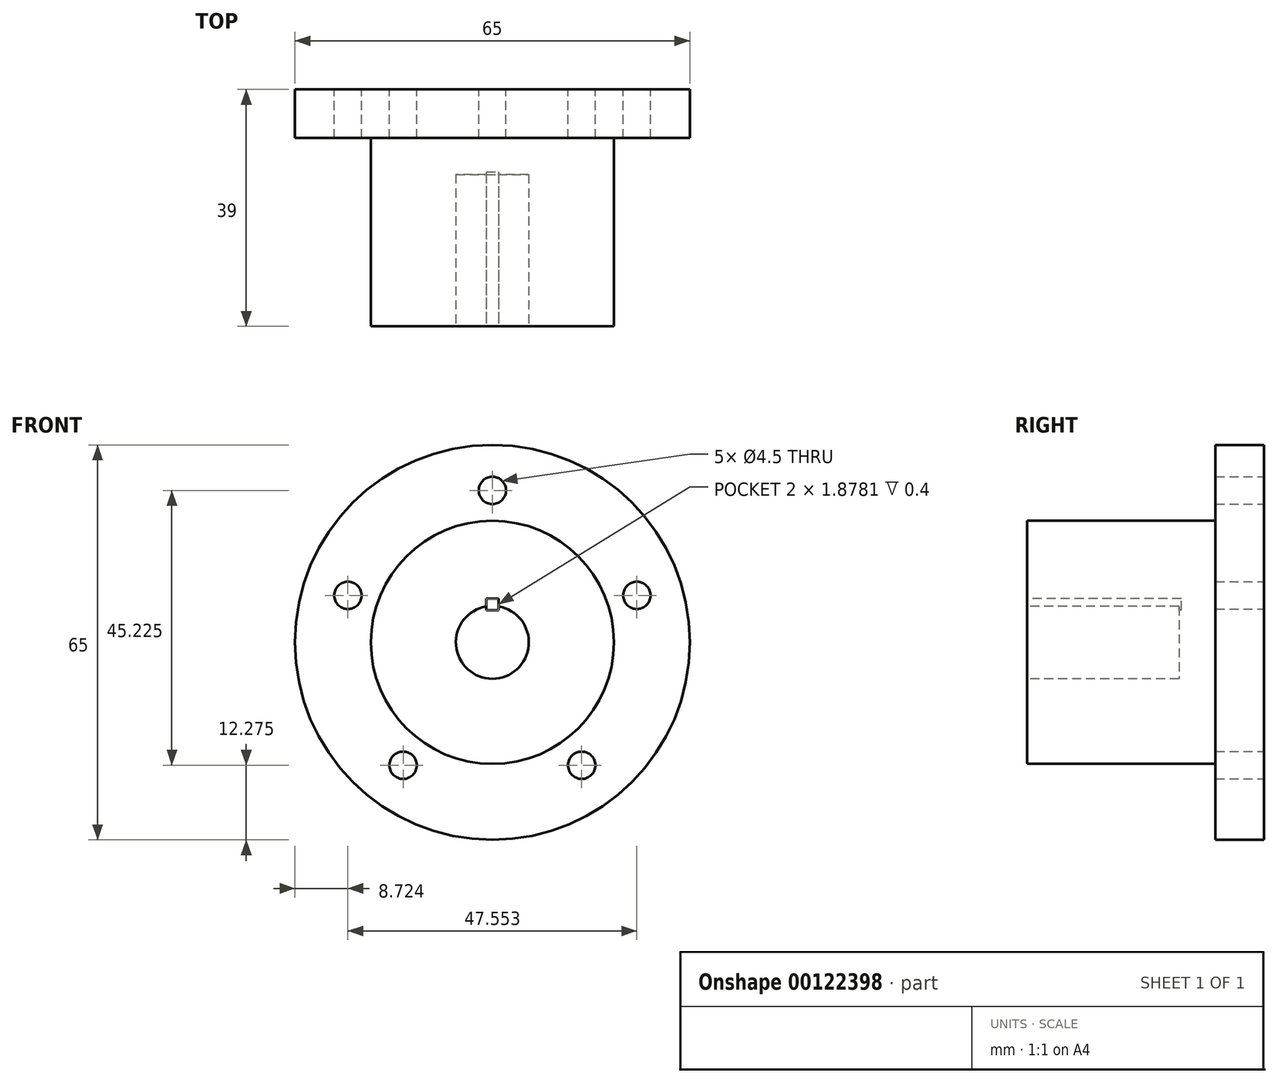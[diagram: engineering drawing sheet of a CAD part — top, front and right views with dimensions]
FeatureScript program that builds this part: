
annotation { "Feature Type Name" : "Feature", "Feature Type Description" : "" }
export const myFeature = defineFeature(function(context is Context, id is Id, definition is map)
    precondition{}
    {
        {
            var Q0;
            Q0=qCreatedBy(makeId("Front.planeOp"),FACE);
            var sketch = newSketch(context, id + "F0", { "sketchPlane" : qUnion([Q0])});
            skCircle(sketch, "E0", {"center": v(0, 0) * mm, "radius": 32.5 * mm});
            skSolve(sketch);
        }
        {
            var Q0;
            Q0=makeQuery(id+"F0.imprint","IMPRINT",FACE,{"disambiguationData":[TD([[makeQuery(id+"F0.imprint","IMPRINT",EDGE,{"derivedFrom":sQuery(id+"F0.wireOp",EDGE,"E0")}),1.0]])]});
            extrude(context, id + "F1", {"entities" : qUnion([Q0]), "depth" : 8 * mm});
        }
        {
            var Q0;
            Q0=makeQuery(id+"F1.opExtrude","CAP_FACE",FACE,{"disambiguationData":[OSD([sQuery(id+"F0.wireOp",EDGE,"E0")])],"isStart":false});
            var sketch = newSketch(context, id + "F2", { "sketchPlane" : qUnion([Q0])});
            skCircle(sketch, "E1", {"center": v(0, 0) * mm, "radius": 20 * mm});
            skSolve(sketch);
        }
        {
            var Q0;
            Q0=makeQuery(id+"F2.imprint","IMPRINT",FACE,{"disambiguationData":[TD([[makeQuery(id+"F2.imprint","IMPRINT",EDGE,{"derivedFrom":sQuery(id+"F2.wireOp",EDGE,"E1")}),1.0]])]});
            extrude(context, id + "F3", {"entities" : qUnion([Q0]), "operationType" : NewBodyOperationType.ADD, "depth" : 31 * mm});
        }
        {
            var Q0;
            Q0=makeQuery(id+"F3.opExtrude","CAP_FACE",FACE,{"disambiguationData":[OSD([sQuery(id+"F2.wireOp",EDGE,"E1")])],"isStart":false});
            var sketch = newSketch(context, id + "F4", { "sketchPlane" : qUnion([Q0])});
            skCircle(sketch, "E2", {"center": v(0, 0) * mm, "radius": 6 * mm});
            skSolve(sketch);
        }
        {
            var Q0;
            Q0=makeQuery(id+"F4.imprint","IMPRINT",FACE,{"disambiguationData":[TD([[makeQuery(id+"F4.imprint","IMPRINT",EDGE,{"derivedFrom":sQuery(id+"F4.wireOp",EDGE,"E2")}),1.0]])]});
            extrude(context, id + "F5", {"entities" : qUnion([Q0]), "operationType" : NewBodyOperationType.REMOVE, "oppositeDirection" : true, "depth" : 25 * mm});
        }
        {
            var Q0;
            Q0=makeQuery(id+"F3.opExtrude","CAP_FACE",FACE,{"disambiguationData":[OSD([sQuery(id+"F2.wireOp",EDGE,"E1")])],"isStart":false});
            var sketch = newSketch(context, id + "F6", { "sketchPlane" : qUnion([Q0])});
            skCircle(sketch, "E3.0", {"center": v(0, 0) * mm, "radius": 6 * mm, "construction": true});
            skLineSegment(sketch, "E4", {"start": v(0, 0) * mm, "end": v(0, 6) * mm, "construction": true});
            skLineSegment(sketch, "E5", {"start": v(0, 5.29) * mm, "end": v(1, 5.29) * mm});
            skLineSegment(sketch, "E6", {"start": v(1, 5.29) * mm, "end": v(1, 7.17) * mm});
            skLineSegment(sketch, "E7", {"start": v(0, 5.29) * mm, "end": v(-1, 5.29) * mm});
            skLineSegment(sketch, "E8", {"start": v(-1, 5.29) * mm, "end": v(-1, 7.17) * mm});
            skLineSegment(sketch, "E9", {"start": v(-1, 7.17) * mm, "end": v(1, 7.17) * mm});
            skSolve(sketch);
        }
        {
            var Q0;
            Q0 = qSketchRegion(id + "F6", true);
            extrude(context, id + "F7", {"entities" : qUnion([Q0]), "operationType" : NewBodyOperationType.REMOVE, "oppositeDirection" : true, "depth" : 25.4 * mm});
        }
        {
            var Q0;
            Q0=makeQuery(id+"F1.opExtrude","CAP_FACE",FACE,{"disambiguationData":[OSD([sQuery(id+"F0.wireOp",EDGE,"E0")])],"isStart":true});
            var sketch = newSketch(context, id + "F8", { "sketchPlane" : qUnion([Q0])});
            skLineSegment(sketch, "E10", {"start": v(0, 0) * mm, "end": v(0, 25) * mm, "construction": true});
            skCircle(sketch, "E11", {"center": v(0, 25) * mm, "radius": 2.25 * mm});
            skCircle(sketch, "E12.1.0", {"center": v(-23.78, 7.73) * mm, "radius": 2.25 * mm});
            skCircle(sketch, "E12.2.0", {"center": v(-14.7, -20.23) * mm, "radius": 2.25 * mm});
            skCircle(sketch, "E12.3.0", {"center": v(14.7, -20.23) * mm, "radius": 2.25 * mm});
            skCircle(sketch, "E12.4.0", {"center": v(23.78, 7.73) * mm, "radius": 2.25 * mm});
            skPoint(sketch, "E12.center", {"position": v(0, 0) * mm});
            skSolve(sketch);
        }
        {
            var Q0;
            Q0 = qSketchRegion(id + "F8", true);
            extrude(context, id + "F9", {"entities" : qUnion([Q0]), "operationType" : NewBodyOperationType.REMOVE, "endBound" : BoundingType.UP_TO_NEXT, "oppositeDirection" : true, "depth" : 25.4 * mm});
        }
    });
